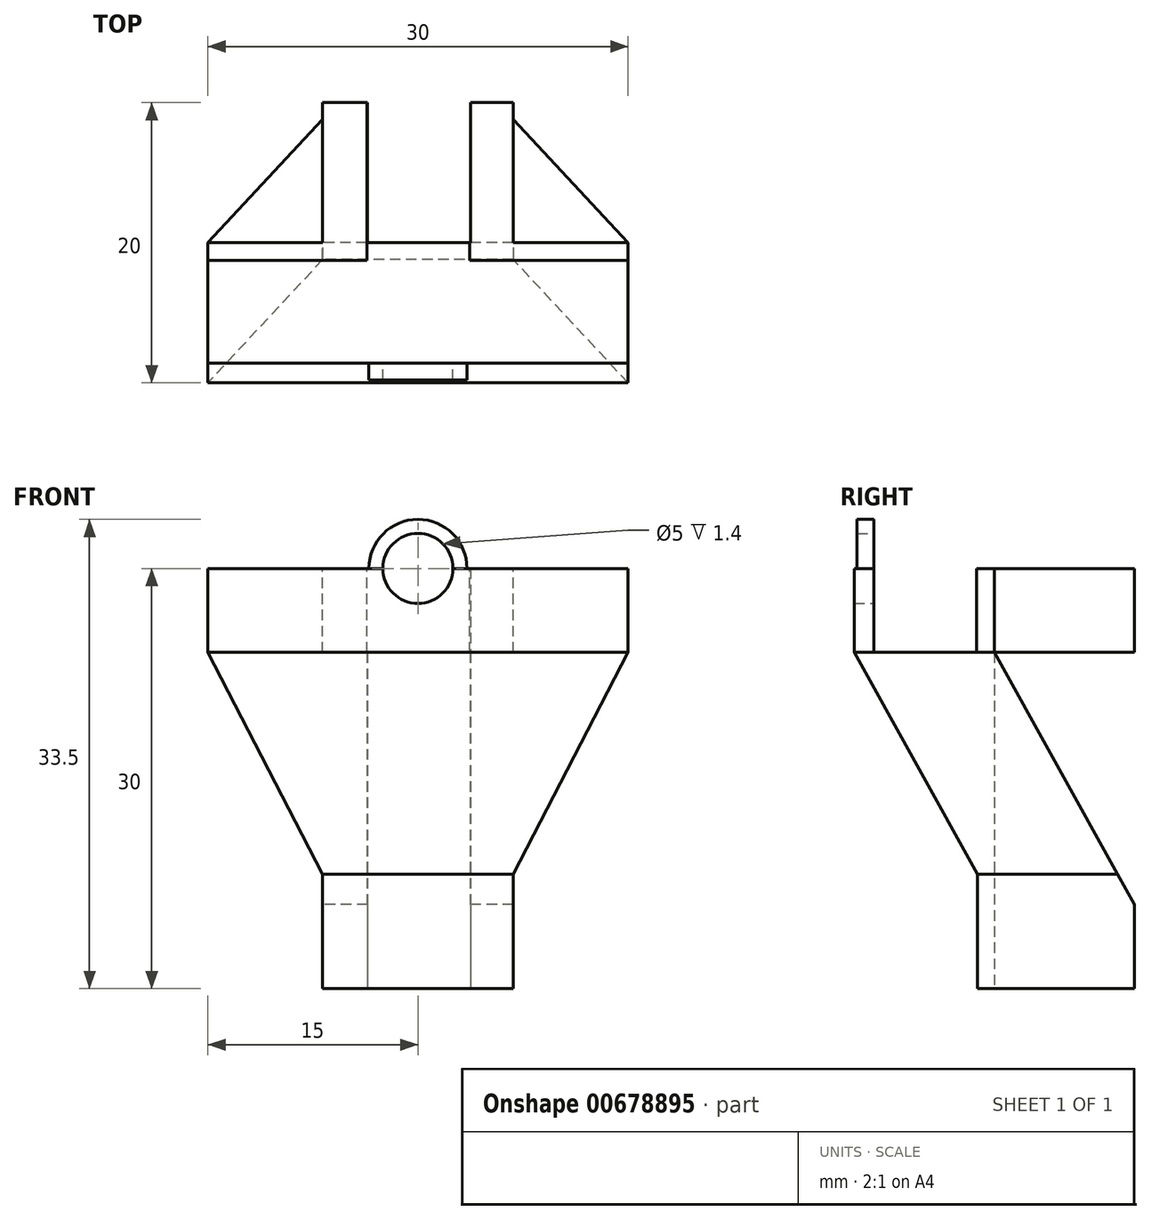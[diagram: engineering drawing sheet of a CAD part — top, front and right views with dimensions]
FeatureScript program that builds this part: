
annotation { "Feature Type Name" : "Feature", "Feature Type Description" : "" }
export const myFeature = defineFeature(function(context is Context, id is Id, definition is map)
    precondition{}
    {
        {
            var Q0;
            Q0=qCreatedBy(makeId("Right.planeOp"),FACE);
            var sketch = newSketch(context, id + "F0", { "sketchPlane" : qUnion([Q0])});
            skLineSegment(sketch, "E0.bottom", {"start": v(-20, 30) * mm, "end": v(0, 30) * mm});
            skLineSegment(sketch, "E0.top", {"start": v(-20, 0) * mm, "end": v(0, 0) * mm});
            skLineSegment(sketch, "E0.left", {"start": v(-20, 30) * mm, "end": v(-20, 0) * mm});
            skLineSegment(sketch, "E0.right", {"start": v(0, 30) * mm, "end": v(0, 0) * mm});
            skLineSegment(sketch, "E1.bottom", {"start": v(-8.8, 6) * mm, "end": v(-1.2, 6) * mm});
            skLineSegment(sketch, "E1.top", {"start": v(-8.8, 0) * mm, "end": v(-1.2, 0) * mm});
            skLineSegment(sketch, "E1.left", {"start": v(-8.8, 6) * mm, "end": v(-8.8, 0) * mm});
            skLineSegment(sketch, "E1.right", {"start": v(-1.2, 6) * mm, "end": v(-1.2, 0) * mm});
            skLineSegment(sketch, "E2.bottom", {"start": v(-18.6, 30) * mm, "end": v(-11.25, 30) * mm});
            skLineSegment(sketch, "E2.top", {"start": v(-18.6, 24) * mm, "end": v(-11.25, 24) * mm});
            skLineSegment(sketch, "E2.left", {"start": v(-18.6, 30) * mm, "end": v(-18.6, 24) * mm});
            skLineSegment(sketch, "E2.right", {"start": v(-11.25, 30) * mm, "end": v(-11.25, 24) * mm});
            skLineSegment(sketch, "E3", {"start": v(-10, 30) * mm, "end": v(-10, 24) * mm});
            skLineSegment(sketch, "E4", {"start": v(0, 0) * mm, "end": v(0, 6) * mm});
            skLineSegment(sketch, "E5", {"start": v(-10, 24) * mm, "end": v(0, 6) * mm});
            skLineSegment(sketch, "E6", {"start": v(-11.25, 24) * mm, "end": v(-1.2, 6) * mm});
            skLineSegment(sketch, "E7", {"start": v(-18.6, 24) * mm, "end": v(-8.8, 6) * mm});
            skLineSegment(sketch, "E8", {"start": v(-10, 0) * mm, "end": v(-10, 6) * mm});
            skLineSegment(sketch, "E9", {"start": v(-20, 30) * mm, "end": v(-20, 24) * mm});
            skLineSegment(sketch, "E10", {"start": v(-20, 24) * mm, "end": v(-10, 6) * mm});
            skLineSegment(sketch, "E11.bottom", {"start": v(0, 6) * mm, "end": v(43.83, 6) * mm});
            skLineSegment(sketch, "E11.top", {"start": v(0, 51.06) * mm, "end": v(43.83, 51.06) * mm});
            skLineSegment(sketch, "E11.left", {"start": v(0, 6) * mm, "end": v(0, 51.06) * mm});
            skLineSegment(sketch, "E11.right", {"start": v(43.83, 6) * mm, "end": v(43.83, 51.06) * mm});
            skSolve(sketch);
        }
        {
            var Q0;
            {var subQ1=sQuery(id+"F0.wireOp",EDGE,"E1.left");Q0=makeQuery(id+"F0.imprint","IMPRINT",FACE,{"disambiguationData":[TD([[makeQuery(id+"F0.imprint","IMPRINT",EDGE,{"derivedFrom":subQ1}),-1.0]])]});}
            var Q1;
            Q1=makeQuery(id+"F0.imprint","IMPRINT",FACE,{"disambiguationData":[TD([[makeQuery(id+"F0.imprint","IMPRINT",EDGE,{"derivedFrom":sQuery(id+"F0.wireOp",EDGE,"E1.bottom")}),1.0]])]});
            var Q2;
            {var subQ3=sQuery(id+"F0.wireOp",EDGE,"E1.right");Q2=makeQuery(id+"F0.imprint","IMPRINT",FACE,{"disambiguationData":[TD([[makeQuery(id+"F0.imprint","IMPRINT",EDGE,{"derivedFrom":subQ3}),1.0]])]});}
            var Q3;
            Q3=makeQuery(id+"F0.imprint","IMPRINT",FACE,{"disambiguationData":[TD([[makeQuery(id+"F0.imprint","IMPRINT",EDGE,{"derivedFrom":sQuery(id+"F0.wireOp",EDGE,"E1.bottom")}),-1.0]])]});
            extrude(context, id + "F1", {"entities" : qUnion([Q0, Q1, Q2, Q3]), "depth" : 30 * mm, "offsetDistance" : 25 * mm});
        }
        {
            var Q0;
            Q0=makeQuery(id+"F1.opExtrude","SWEPT_FACE",FACE,{"disambiguationData":[OSD([sQuery(id+"F0.wireOp",EDGE,"E0.top"),sQuery(id+"F0.wireOp",EDGE,"E1.top")])]});
            var sketch = newSketch(context, id + "F2", { "sketchPlane" : qUnion([Q0])});
            skLineSegment(sketch, "E12", {"start": v(10.2, 10) * mm, "end": v(10.2, 0) * mm});
            skLineSegment(sketch, "E13", {"start": v(11.4, 10) * mm, "end": v(11.4, 0) * mm});
            skLineSegment(sketch, "E14", {"start": v(18.75, 10) * mm, "end": v(18.75, 0) * mm});
            skLineSegment(sketch, "E15", {"start": v(19.95, 10) * mm, "end": v(19.95, 0) * mm});
            skLineSegment(sketch, "E16", {"start": v(10.2, 10) * mm, "end": v(11.4, 10) * mm});
            skLineSegment(sketch, "E17", {"start": v(18.75, 10) * mm, "end": v(11.4, 10) * mm});
            skLineSegment(sketch, "E18", {"start": v(19.95, 10) * mm, "end": v(18.75, 10) * mm});
            skLineSegment(sketch, "E19", {"start": v(19.95, 0) * mm, "end": v(18.75, 0) * mm});
            skLineSegment(sketch, "E20", {"start": v(11.4, 0) * mm, "end": v(10.2, 0) * mm});
            skLineSegment(sketch, "E21", {"start": v(0, 11.2) * mm, "end": v(30, 11.2) * mm});
            skLineSegment(sketch, "E22", {"start": v(0, 11.2) * mm, "end": v(0, 10) * mm});
            skLineSegment(sketch, "E23", {"start": v(0, 10) * mm, "end": v(30, 10) * mm});
            skLineSegment(sketch, "E24", {"start": v(30, 10) * mm, "end": v(30, 11.2) * mm});
            skLineSegment(sketch, "E25", {"start": v(10.2, 10) * mm, "end": v(10.2, 11.2) * mm});
            skLineSegment(sketch, "E26", {"start": v(10.2, 11.2) * mm, "end": v(11.4, 11.2) * mm});
            skLineSegment(sketch, "E27", {"start": v(11.4, 11.2) * mm, "end": v(11.4, 10) * mm});
            skLineSegment(sketch, "E28", {"start": v(18.75, 10) * mm, "end": v(18.75, 11.2) * mm});
            skLineSegment(sketch, "E29", {"start": v(19.95, 10) * mm, "end": v(19.95, 11.2) * mm});
            skLineSegment(sketch, "E30", {"start": v(19.95, 11.2) * mm, "end": v(18.75, 11.2) * mm});
            skSolve(sketch);
        }
        {
            var Q0;
            Q0=makeQuery(id+"F2.imprint","IMPRINT",FACE,{"disambiguationData":[TD([[makeQuery(id+"F2.imprint","IMPRINT",EDGE,{"derivedFrom":sQuery(id+"F2.wireOp",EDGE,"E21")}),-1.0]])]});
            var Q1;
            {var subQ0=sQuery(id+"F2.wireOp",EDGE,"E25");Q1=makeQuery(id+"F2.imprint","IMPRINT",FACE,{"disambiguationData":[TD([[makeQuery(id+"F2.imprint","IMPRINT",EDGE,{"derivedFrom":subQ0}),-1.0]])]});}
            var Q2;
            {var subQ0=sQuery(id+"F2.wireOp",EDGE,"E28");Q2=makeQuery(id+"F2.imprint","IMPRINT",FACE,{"disambiguationData":[TD([[makeQuery(id+"F2.imprint","IMPRINT",EDGE,{"derivedFrom":subQ0}),-1.0]])]});}
            extrude(context, id + "F3", {"entities" : qUnion([Q0, Q1, Q2]), "operationType" : NewBodyOperationType.ADD, "depth" : -10 * mm, "offsetDistance" : 25 * mm});
        }
        {
            var Q0;
            Q0=makeQuery(id+"F1.opExtrude","SWEPT_FACE",FACE,{"disambiguationData":[OSD([sQuery(id+"F0.wireOp",EDGE,"E3")])]});
            var sketch = newSketch(context, id + "F4", { "sketchPlane" : qUnion([Q0])});
            skLineSegment(sketch, "E31", {"start": v(-21.8, 24) * mm, "end": v(-21.8, 30) * mm});
            skLineSegment(sketch, "E32", {"start": v(-18.7, 24) * mm, "end": v(-18.7, 30) * mm});
            skLineSegment(sketch, "E33", {"start": v(-11.35, 24) * mm, "end": v(-11.35, 30) * mm});
            skLineSegment(sketch, "E34", {"start": v(-8.2, 24) * mm, "end": v(-8.2, 30) * mm});
            skLineSegment(sketch, "E35", {"start": v(-21.8, 30) * mm, "end": v(-18.7, 30) * mm});
            skLineSegment(sketch, "E36", {"start": v(-21.8, 24) * mm, "end": v(-18.7, 24) * mm});
            skLineSegment(sketch, "E37", {"start": v(-11.35, 24) * mm, "end": v(-8.2, 24) * mm});
            skLineSegment(sketch, "E38", {"start": v(-8.2, 30) * mm, "end": v(-11.35, 30) * mm});
            skLineSegment(sketch, "E39", {"start": v(-18.7, 30) * mm, "end": v(-21.8, 30) * mm});
            skSolve(sketch);
        }
        {
            var Q0;
            Q0=makeQuery(id+"F4.imprint","IMPRINT",FACE,{"disambiguationData":[TD([[makeQuery(id+"F4.imprint","IMPRINT",EDGE,{"derivedFrom":sQuery(id+"F4.wireOp",EDGE,"E31")}),-1.0]])]});
            var Q1;
            Q1=makeQuery(id+"F4.imprint","IMPRINT",FACE,{"disambiguationData":[TD([[makeQuery(id+"F4.imprint","IMPRINT",EDGE,{"derivedFrom":sQuery(id+"F4.wireOp",EDGE,"E33")}),-1.0]])]});
            extrude(context, id + "F5", {"entities" : qUnion([Q0, Q1]), "operationType" : NewBodyOperationType.ADD, "depth" : 25 * mm, "offsetDistance" : 25 * mm});
        }
        {
            var Q0;
            {var subQ0=sQuery(id+"F4.wireOp",EDGE,"E32");Q0=makeQuery(id+"F4.imprint","IMPRINT",FACE,{"disambiguationData":[TD([[makeQuery(id+"F4.imprint","IMPRINT",EDGE,{"derivedFrom":subQ0}),-1.0]])]});}
            extrude(context, id + "F6", {"entities" : qUnion([Q0]), "operationType" : NewBodyOperationType.REMOVE, "oppositeDirection" : true, "depth" : 3 * mm, "offsetDistance" : 25 * mm});
        }
        {
            var Q0;
            {var subQ0=sQuery(id+"F2.wireOp",EDGE,"E13");Q0=makeQuery(id+"F2.imprint","IMPRINT",FACE,{"disambiguationData":[TD([[makeQuery(id+"F2.imprint","IMPRINT",EDGE,{"derivedFrom":subQ0}),1.0]])]});}
            extrude(context, id + "F7", {"entities" : qUnion([Q0]), "operationType" : NewBodyOperationType.REMOVE, "oppositeDirection" : true, "depth" : 30.8 * mm, "offsetDistance" : 25 * mm});
        }
        {
            var Q0;
            {var subQ3=sQuery(id+"F0.wireOp",EDGE,"E11.bottom");Q0=makeQuery(id+"F0.imprint","IMPRINT",FACE,{"disambiguationData":[TD([[makeQuery(id+"F0.imprint","IMPRINT",EDGE,{"derivedFrom":subQ3}),1.0]])]});}
            extrude(context, id + "F8", {"entities" : qUnion([Q0]), "operationType" : NewBodyOperationType.REMOVE, "depth" : 25 * mm, "offsetDistance" : 25 * mm});
        }
        {
            var Q0;
            Q0=makeQuery(id+"F3.opExtrude","SWEPT_FACE",FACE,{"disambiguationData":[OSD([sQuery(id+"F2.wireOp",EDGE,"E21"),sQuery(id+"F2.wireOp",EDGE,"E26"),sQuery(id+"F2.wireOp",EDGE,"E30")])]});
            var sketch = newSketch(context, id + "F9", { "sketchPlane" : qUnion([Q0])});
            skLineSegment(sketch, "E40", {"start": v(10.2, 8.16) * mm, "end": v(10.2, 0) * mm});
            skLineSegment(sketch, "E41", {"start": v(11.4, 0) * mm, "end": v(11.4, 8.16) * mm});
            skLineSegment(sketch, "E42", {"start": v(18.6, 0) * mm, "end": v(18.6, 8.16) * mm});
            skLineSegment(sketch, "E43", {"start": v(19.8, 0) * mm, "end": v(19.8, 8.16) * mm});
            skLineSegment(sketch, "E44", {"start": v(19.8, 8.16) * mm, "end": v(18.6, 8.16) * mm});
            skLineSegment(sketch, "E45", {"start": v(18.6, 0) * mm, "end": v(19.8, 0) * mm});
            skLineSegment(sketch, "E46", {"start": v(11.4, 0) * mm, "end": v(10.2, 0) * mm});
            skLineSegment(sketch, "E47", {"start": v(11.4, 8.16) * mm, "end": v(10.2, 8.16) * mm});
            skLineSegment(sketch, "E48", {"start": v(10.2, 0) * mm, "end": v(11.4, 0) * mm});
            skLineSegment(sketch, "E49", {"start": v(10.2, 0) * mm, "end": v(8.2, 0) * mm});
            skLineSegment(sketch, "E50", {"start": v(8.2, 0) * mm, "end": v(8.2, 8.16) * mm});
            skLineSegment(sketch, "E51", {"start": v(8.2, 8.16) * mm, "end": v(10.2, 8.16) * mm});
            skLineSegment(sketch, "E52", {"start": v(19.8, 0) * mm, "end": v(21.8, 0) * mm});
            skLineSegment(sketch, "E53", {"start": v(21.8, 0) * mm, "end": v(21.8, 8.16) * mm});
            skLineSegment(sketch, "E54", {"start": v(21.8, 8.16) * mm, "end": v(19.8, 8.16) * mm});
            skSolve(sketch);
        }
        {
            var Q0;
            {var subQ0=sQuery(id+"F9.wireOp",EDGE,"E50");Q0=makeQuery(id+"F9.imprint","IMPRINT",FACE,{"disambiguationData":[TD([[makeQuery(id+"F9.imprint","IMPRINT",EDGE,{"derivedFrom":subQ0}),1.0]])]});}
            var Q1;
            {var subQ0=sQuery(id+"F9.wireOp",EDGE,"E53");Q1=makeQuery(id+"F9.imprint","IMPRINT",FACE,{"disambiguationData":[TD([[makeQuery(id+"F9.imprint","IMPRINT",EDGE,{"derivedFrom":subQ0}),-1.0]])]});}
            extrude(context, id + "F10", {"entities" : qUnion([Q0, Q1]), "operationType" : NewBodyOperationType.REMOVE, "oppositeDirection" : true, "depth" : 25 * mm, "offsetDistance" : 25 * mm});
        }
        {
            var Q0;
            Q0=qCreatedBy(makeId("Front.planeOp"),FACE);
            var sketch = newSketch(context, id + "F11", { "sketchPlane" : qUnion([Q0])});
            skLineSegment(sketch, "E55", {"start": v(0, 0) * mm, "end": v(0, 8.16) * mm});
            skLineSegment(sketch, "E56", {"start": v(0, 8.16) * mm, "end": v(8.2, 8.16) * mm});
            skLineSegment(sketch, "E57", {"start": v(8.2, 8.16) * mm, "end": v(0, 24) * mm});
            skLineSegment(sketch, "E58", {"start": v(0, 24) * mm, "end": v(0, 8.16) * mm});
            skLineSegment(sketch, "E59", {"start": v(8.2, 8.16) * mm, "end": v(11.4, 8.16) * mm});
            skLineSegment(sketch, "E60", {"start": v(11.4, 8.16) * mm, "end": v(18.6, 8.16) * mm});
            skLineSegment(sketch, "E61", {"start": v(18.6, 8.16) * mm, "end": v(21.8, 8.16) * mm});
            skLineSegment(sketch, "E62", {"start": v(21.8, 8.16) * mm, "end": v(30, 8.16) * mm});
            skLineSegment(sketch, "E63", {"start": v(30, 8.16) * mm, "end": v(30, 24) * mm});
            skLineSegment(sketch, "E64", {"start": v(30, 24) * mm, "end": v(21.8, 8.16) * mm});
            skSolve(sketch);
        }
        {
            var Q0;
            Q0 = qSketchRegion(id + "F11", true);
            extrude(context, id + "F12", {"entities" : qUnion([Q0]), "operationType" : NewBodyOperationType.REMOVE, "depth" : 25 * mm, "offsetDistance" : 25 * mm});
        }
        {
            var Q0;
            Q0=makeQuery(id+"F1.opExtrude","SWEPT_FACE",FACE,{"disambiguationData":[OSD([sQuery(id+"F0.wireOp",EDGE,"E2.left")])]});
            var sketch = newSketch(context, id + "F13", { "sketchPlane" : qUnion([Q0])});
            skLineSegment(sketch, "E65", {"start": v(-30, 29.2) * mm, "end": v(-15, 29.2) * mm});
            skCircle(sketch, "E66", {"center": v(-15, 30) * mm, "radius": 2.5 * mm});
            skCircle(sketch, "E67", {"center": v(-15, 30) * mm, "radius": 3.5 * mm});
            skSolve(sketch);
        }
        {
            var Q0;
            {var subQ0=sQuery(id+"F13.wireOp",EDGE,"E66");var subQ1=makeQuery(id+"F1.opExtrude","SWEPT_EDGE",EDGE,{"disambiguationData":[OSD([sQuery(id+"F0.wireOp",EDGE,"E0.bottom"),sQuery(id+"F0.wireOp",EDGE,"E2.bottom"),sQuery(id+"F0.wireOp",EDGE,"E2.left")])]});var subQ2=makeQuery(id+"F13.imprint","INTERSECT",VERTEX,{"disambiguationData":[OD(0.0)],"derivedFrom":[subQ1,subQ0]});Q0=makeQuery(id+"F13.imprint","IMPRINT",FACE,{"disambiguationData":[TD([[makeQuery(id+"F13.imprint","IMPRINT",EDGE,{"disambiguationData":[TD([[subQ2,1.0]])],"derivedFrom":subQ0}),1.0]])]});}
            var Q1;
            {var subQ0=sQuery(id+"F13.wireOp",EDGE,"E66");var subQ1=makeQuery(id+"F13.imprint","INTERSECT",VERTEX,{"derivedFrom":[sQuery(id+"F13.wireOp",EDGE,"E65"),subQ0]});Q1=makeQuery(id+"F13.imprint","IMPRINT",FACE,{"disambiguationData":[TD([[makeQuery(id+"F13.imprint","IMPRINT",EDGE,{"disambiguationData":[TD([[subQ1,1.0]])],"derivedFrom":subQ0}),1.0]])]});}
            extrude(context, id + "F14", {"entities" : qUnion([Q0, Q1]), "operationType" : NewBodyOperationType.REMOVE, "oppositeDirection" : true, "depth" : 25 * mm, "offsetDistance" : 25 * mm});
        }
        {
            var Q0;
            Q0 = qSketchRegion(id + "F13", true);
            extrude(context, id + "F15", {"entities" : qUnion([Q0]), "operationType" : NewBodyOperationType.ADD, "oppositeDirection" : true, "depth" : 1.2 * mm, "offsetDistance" : 25 * mm});
        }
    });
